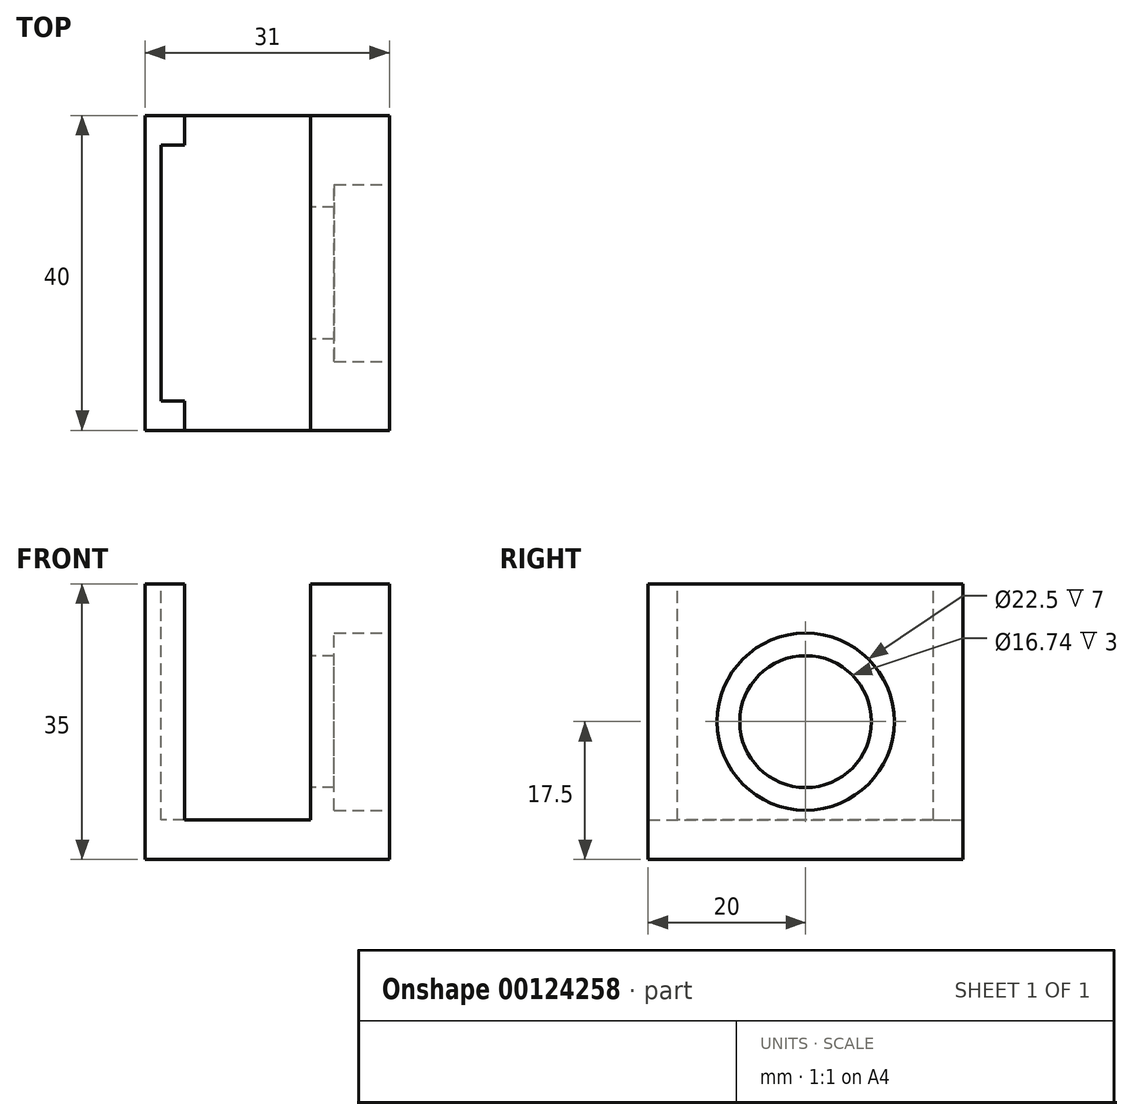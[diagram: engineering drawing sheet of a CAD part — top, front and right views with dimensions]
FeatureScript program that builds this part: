
annotation { "Feature Type Name" : "Feature", "Feature Type Description" : "" }
export const myFeature = defineFeature(function(context is Context, id is Id, definition is map)
    precondition{}
    {
        {
            var Q0;
            Q0=qCreatedBy(makeId("Front.planeOp"),FACE);
            var sketch = newSketch(context, id + "F0", { "sketchPlane" : qUnion([Q0])});
            skLineSegment(sketch, "E0", {"start": v(-30, 35) * mm, "end": v(-30, 0) * mm});
            skLineSegment(sketch, "E1", {"start": v(-30, 0) * mm, "end": v(1, 0) * mm});
            skLineSegment(sketch, "E2", {"start": v(1, 0) * mm, "end": v(1, 35) * mm});
            skLineSegment(sketch, "E3", {"start": v(1, 35) * mm, "end": v(-9, 35) * mm});
            skLineSegment(sketch, "E4", {"start": v(-9, 35) * mm, "end": v(-9, 5) * mm});
            skLineSegment(sketch, "E5", {"start": v(-9, 5) * mm, "end": v(-25, 5) * mm});
            skLineSegment(sketch, "E6", {"start": v(-25, 5) * mm, "end": v(-25, 35) * mm});
            skLineSegment(sketch, "E7", {"start": v(-25, 35) * mm, "end": v(-30, 35) * mm});
            skSolve(sketch);
        }
        {
            var Q0;
            Q0=makeQuery(id+"F0.imprint","IMPRINT",FACE,{"disambiguationData":[TD([[makeQuery(id+"F0.imprint","IMPRINT",EDGE,{"derivedFrom":sQuery(id+"F0.wireOp",EDGE,"E0")}),1.0]])]});
            extrude(context, id + "F1", {"entities" : qUnion([Q0]), "endBound" : BoundingType.SYMMETRIC, "depth" : 40 * mm});
        }
        {
            var Q0;
            Q0=makeQuery(id+"F1.opExtrude","SWEPT_FACE",FACE,{"disambiguationData":[OSD([sQuery(id+"F0.wireOp",EDGE,"E2")])]});
            var sketch = newSketch(context, id + "F2", { "sketchPlane" : qUnion([Q0])});
            skCircle(sketch, "E8", {"center": v(0, 17.5) * mm, "radius": 11.25 * mm});
            skLineSegment(sketch, "E9.0", {"start": v(-20, 5) * mm, "end": v(20, 5) * mm});
            skSolve(sketch);
        }
        {
            var Q0;
            Q0=makeQuery(id+"F2.imprint","IMPRINT",FACE,{"disambiguationData":[TD([[makeQuery(id+"F2.imprint","IMPRINT",EDGE,{"derivedFrom":sQuery(id+"F2.wireOp",EDGE,"E8")}),1.0]])]});
            extrude(context, id + "F3", {"entities" : qUnion([Q0]), "operationType" : NewBodyOperationType.REMOVE, "oppositeDirection" : true, "depth" : 7 * mm});
        }
        {
            var Q0;
            Q0=makeQuery(id+"F3.boolean.opBoolean","COPY",FACE,{"derivedFrom":makeQuery(id+"F3.opExtrude","CAP_FACE",FACE,{"disambiguationData":[OSD([sQuery(id+"F2.wireOp",EDGE,"E8")])],"isStart":false})});
            var sketch = newSketch(context, id + "F4", { "sketchPlane" : qUnion([Q0])});
            skCircle(sketch, "E10", {"center": v(0, 17.5) * mm, "radius": 6.75 * mm});
            skSolve(sketch);
        }
        {
            var Q0;
            Q0=makeQuery(id+"F4.imprint","IMPRINT",FACE,{"disambiguationData":[TD([[makeQuery(id+"F4.imprint","IMPRINT",EDGE,{"derivedFrom":sQuery(id+"F4.wireOp",EDGE,"E10")}),1.0]])]});
            extrude(context, id + "F5", {"entities" : qUnion([Q0]), "operationType" : NewBodyOperationType.REMOVE, "oppositeDirection" : true, "depth" : 5 * mm});
        }
        {
            var Q0;
            Q0=makeQuery(id+"F1.opExtrude","SWEPT_FACE",FACE,{"disambiguationData":[OSD([sQuery(id+"F0.wireOp",EDGE,"E7")])]});
            var sketch = newSketch(context, id + "F6", { "sketchPlane" : qUnion([Q0])});
            skLineSegment(sketch, "E11", {"start": v(-25, 16.25) * mm, "end": v(-28, 16.25) * mm});
            skLineSegment(sketch, "E12", {"start": v(-28, 16.25) * mm, "end": v(-28, -16.25) * mm});
            skLineSegment(sketch, "E13", {"start": v(-28, -16.25) * mm, "end": v(-25, -16.25) * mm});
            skSolve(sketch);
        }
        {
            var Q0;
            {var subQ0=sQuery(id+"F6.wireOp",EDGE,"E11");Q0=makeQuery(id+"F6.imprint","IMPRINT",FACE,{"disambiguationData":[TD([[makeQuery(id+"F6.imprint","IMPRINT",EDGE,{"derivedFrom":subQ0}),1.0]])]});}
            extrude(context, id + "F7", {"entities" : qUnion([Q0]), "operationType" : NewBodyOperationType.REMOVE, "oppositeDirection" : true, "depth" : 30 * mm});
        }
        {
            var Q0;
            Q0=makeQuery(id+"F1.opExtrude","SWEPT_FACE",FACE,{"disambiguationData":[OSD([sQuery(id+"F0.wireOp",EDGE,"E4")])]});
            var sketch = newSketch(context, id + "F8", { "sketchPlane" : qUnion([Q0])});
            skCircle(sketch, "E14.0", {"center": v(0, 17.5) * mm, "radius": 6.75 * mm});
            skCircle(sketch, "E15.cCircle", {"center": v(0, 17.5) * mm, "radius": 7.25 * mm, "construction": true});
            skLineSegment(sketch, "E15.0", {"start": v(-4.19, 24.75) * mm, "end": v(4.19, 24.75) * mm});
            skLineSegment(sketch, "E15.1", {"start": v(4.19, 24.75) * mm, "end": v(8.37, 17.5) * mm});
            skLineSegment(sketch, "E15.2", {"start": v(8.37, 17.5) * mm, "end": v(4.19, 10.25) * mm});
            skLineSegment(sketch, "E15.3", {"start": v(4.19, 10.25) * mm, "end": v(-4.19, 10.25) * mm});
            skLineSegment(sketch, "E15.4", {"start": v(-4.19, 10.25) * mm, "end": v(-8.37, 17.5) * mm});
            skLineSegment(sketch, "E15.5", {"start": v(-8.37, 17.5) * mm, "end": v(-4.19, 24.75) * mm});
            skPoint(sketch, "E15.0.midPoint", {"position": v(0, 24.75) * mm});
            skCircle(sketch, "E16", {"center": v(0, 17.5) * mm, "radius": 8.37 * mm});
            skSolve(sketch);
        }
        {
            var Q0;
            {var subQ0=sQuery(id+"F8.wireOp",EDGE,"E15.1");Q0=makeQuery(id+"F8.imprint","IMPRINT",FACE,{"disambiguationData":[TD([[makeQuery(id+"F8.imprint","IMPRINT",EDGE,{"derivedFrom":subQ0}),1.0]])]});}
            var Q1;
            {var subQ0=sQuery(id+"F8.wireOp",EDGE,"E15.2");Q1=makeQuery(id+"F8.imprint","IMPRINT",FACE,{"disambiguationData":[TD([[makeQuery(id+"F8.imprint","IMPRINT",EDGE,{"derivedFrom":subQ0}),1.0]])]});}
            var Q2;
            {var subQ0=sQuery(id+"F8.wireOp",EDGE,"E15.3");Q2=makeQuery(id+"F8.imprint","IMPRINT",FACE,{"disambiguationData":[TD([[makeQuery(id+"F8.imprint","IMPRINT",EDGE,{"derivedFrom":subQ0}),1.0]])]});}
            var Q3;
            {var subQ0=sQuery(id+"F8.wireOp",EDGE,"E15.4");Q3=makeQuery(id+"F8.imprint","IMPRINT",FACE,{"disambiguationData":[TD([[makeQuery(id+"F8.imprint","IMPRINT",EDGE,{"derivedFrom":subQ0}),1.0]])]});}
            var Q4;
            {var subQ0=sQuery(id+"F8.wireOp",EDGE,"E15.5");Q4=makeQuery(id+"F8.imprint","IMPRINT",FACE,{"disambiguationData":[TD([[makeQuery(id+"F8.imprint","IMPRINT",EDGE,{"derivedFrom":subQ0}),1.0]])]});}
            var Q5;
            {var subQ0=sQuery(id+"F8.wireOp",EDGE,"E15.0");Q5=makeQuery(id+"F8.imprint","IMPRINT",FACE,{"disambiguationData":[TD([[makeQuery(id+"F8.imprint","IMPRINT",EDGE,{"derivedFrom":subQ0}),1.0]])]});}
            var Q6;
            Q6=makeQuery(id+"F8.imprint","IMPRINT",FACE,{"disambiguationData":[TD([[makeQuery(id+"F8.imprint","IMPRINT",EDGE,{"derivedFrom":sQuery(id+"F8.wireOp",EDGE,"E14.0")}),1.0]])]});
            extrude(context, id + "F9", {"entities" : qUnion([Q0, Q1, Q2, Q3, Q4, Q5, Q6]), "operationType" : NewBodyOperationType.REMOVE, "oppositeDirection" : true, "depth" : 25 * mm});
        }
    });
